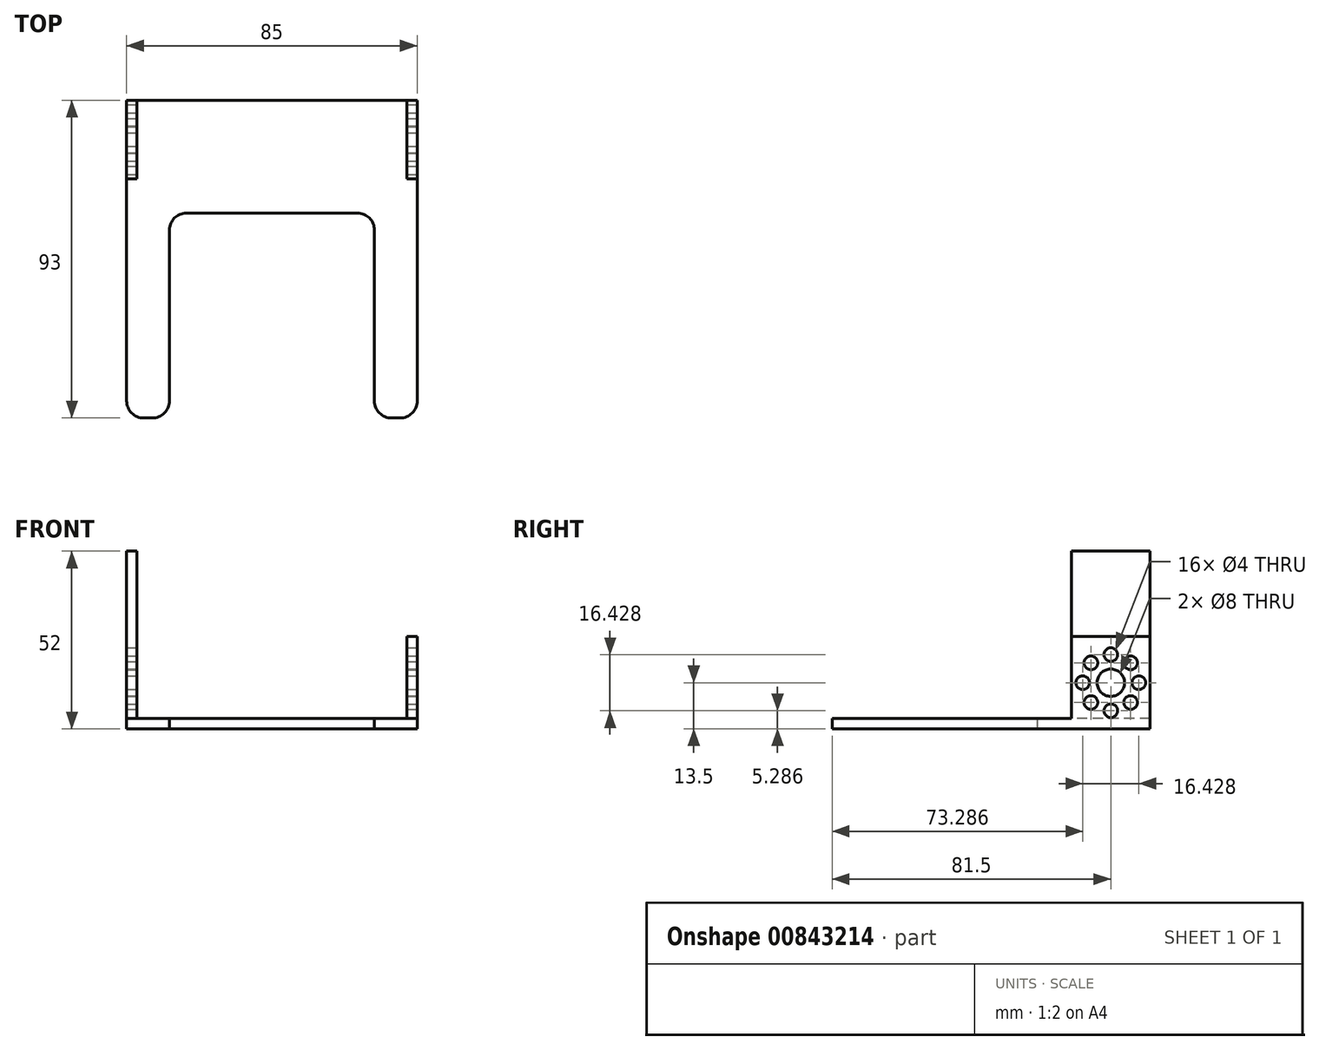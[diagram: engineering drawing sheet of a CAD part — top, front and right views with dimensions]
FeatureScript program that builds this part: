
annotation { "Feature Type Name" : "Feature", "Feature Type Description" : "" }
export const myFeature = defineFeature(function(context is Context, id is Id, definition is map)
    precondition{}
    {
        {
            var Q0;
            Q0=qCreatedBy(makeId("Top.planeOp"),FACE);
            var sketch = newSketch(context, id + "F0", { "sketchPlane" : qUnion([Q0])});
            skLineSegment(sketch, "E0.bottom", {"start": v(0, 0) * mm, "end": v(85, 0) * mm});
            skLineSegment(sketch, "E0.top", {"start": v(0, 23) * mm, "end": v(85, 23) * mm});
            skLineSegment(sketch, "E0.left", {"start": v(0, 0) * mm, "end": v(0, 23) * mm});
            skLineSegment(sketch, "E0.right", {"start": v(85, 0) * mm, "end": v(85, 23) * mm});
            skLineSegment(sketch, "E1.top", {"start": v(17.5, -10) * mm, "end": v(67.5, -10) * mm});
            skLineSegment(sketch, "E1.left", {"start": v(0, 0) * mm, "end": v(0, -10) * mm});
            skLineSegment(sketch, "E1.right", {"start": v(85, 0) * mm, "end": v(85, -10) * mm});
            skLineSegment(sketch, "E2.top", {"start": v(5, -70) * mm, "end": v(7.5, -70) * mm});
            skLineSegment(sketch, "E2.left", {"start": v(0, -10) * mm, "end": v(0, -65) * mm});
            skLineSegment(sketch, "E2.right", {"start": v(12.5, -15) * mm, "end": v(12.5, -65) * mm});
            skLineSegment(sketch, "E3.top", {"start": v(80, -70) * mm, "end": v(77.5, -70) * mm});
            skLineSegment(sketch, "E3.left", {"start": v(85, -10) * mm, "end": v(85, -65) * mm});
            skLineSegment(sketch, "E3.right", {"start": v(72.5, -15) * mm, "end": v(72.5, -65) * mm});
            skPoint(sketch, "E4.visualSharp", {"position": v(12.5, -70) * mm});
            skArc(sketch, "E4.filletArc", {"start": v(7.5, -70) * mm, "mid": v(11.04, -68.54) * mm, "end": v(12.5, -65) * mm});
            skPoint(sketch, "E5.visualSharp", {"position": v(0, -70) * mm});
            skArc(sketch, "E5.filletArc", {"start": v(0, -65) * mm, "mid": v(1.46, -68.54) * mm, "end": v(5, -70) * mm});
            skPoint(sketch, "E6.visualSharp", {"position": v(72.5, -70) * mm});
            skArc(sketch, "E6.filletArc", {"start": v(72.5, -65) * mm, "mid": v(73.96, -68.54) * mm, "end": v(77.5, -70) * mm});
            skPoint(sketch, "E7.visualSharp", {"position": v(85, -70) * mm});
            skArc(sketch, "E7.filletArc", {"start": v(80, -70) * mm, "mid": v(83.54, -68.54) * mm, "end": v(85, -65) * mm});
            skPoint(sketch, "E8.visualSharp", {"position": v(12.5, -10) * mm});
            skArc(sketch, "E8.filletArc", {"start": v(17.5, -10) * mm, "mid": v(13.96, -11.46) * mm, "end": v(12.5, -15) * mm});
            skPoint(sketch, "E9.visualSharp", {"position": v(72.5, -10) * mm});
            skArc(sketch, "E9.filletArc", {"start": v(72.5, -15) * mm, "mid": v(71.04, -11.46) * mm, "end": v(67.5, -10) * mm});
            skSolve(sketch);
        }
        {
            var Q0;
            Q0=qSketchRegion(id+"F0",true);
            extrude(context, id + "F1", {"entities" : qUnion([Q0]), "depth" : 3 * mm, "offsetDistance" : 25 * mm});
        }
        {
            var Q0;
            Q0=makeQuery(id+"F1.opExtrude","CAP_FACE",FACE,{"disambiguationData":[OSD([sQuery(id+"F0.wireOp",EDGE,"E0.bottom"),sQuery(id+"F0.wireOp",EDGE,"E0.top"),sQuery(id+"F0.wireOp",EDGE,"E0.left"),sQuery(id+"F0.wireOp",EDGE,"E0.right")])],"isStart":false});
            var sketch = newSketch(context, id + "F2", { "sketchPlane" : qUnion([Q0])});
            skLineSegment(sketch, "E10.bottom", {"start": v(0, 23) * mm, "end": v(3, 23) * mm});
            skLineSegment(sketch, "E10.top", {"start": v(0, 0) * mm, "end": v(3, 0) * mm});
            skLineSegment(sketch, "E10.left", {"start": v(0, 23) * mm, "end": v(0, 0) * mm});
            skLineSegment(sketch, "E10.right", {"start": v(3, 23) * mm, "end": v(3, 0) * mm});
            skLineSegment(sketch, "E11.bottom", {"start": v(85, 23) * mm, "end": v(82, 23) * mm});
            skLineSegment(sketch, "E11.top", {"start": v(85, 0) * mm, "end": v(82, 0) * mm});
            skLineSegment(sketch, "E11.left", {"start": v(85, 23) * mm, "end": v(85, 0) * mm});
            skLineSegment(sketch, "E11.right", {"start": v(82, 23) * mm, "end": v(82, 0) * mm});
            skSolve(sketch);
        }
        {
            var Q0;
            Q0=qSketchRegion(id+"F2",true);
            extrude(context, id + "F3", {"entities" : qUnion([Q0]), "operationType" : NewBodyOperationType.ADD, "depth" : 24 * mm, "offsetDistance" : 25 * mm});
        }
        {
            var Q0;
            Q0=makeQuery(id+"F3.opExtrude","CAP_FACE",FACE,{"disambiguationData":[OSD([sQuery(id+"F2.wireOp",EDGE,"E10.bottom"),sQuery(id+"F2.wireOp",EDGE,"E10.top"),sQuery(id+"F2.wireOp",EDGE,"E10.left"),sQuery(id+"F2.wireOp",EDGE,"E10.right")])],"isStart":false});
            var sketch = newSketch(context, id + "F4", { "sketchPlane" : qUnion([Q0])});
            skLineSegment(sketch, "E12.bottom", {"start": v(0, 23) * mm, "end": v(3, 23) * mm});
            skLineSegment(sketch, "E12.top", {"start": v(0, 0) * mm, "end": v(3, 0) * mm});
            skLineSegment(sketch, "E12.left", {"start": v(0, 23) * mm, "end": v(0, 0) * mm});
            skLineSegment(sketch, "E12.right", {"start": v(3, 23) * mm, "end": v(3, 0) * mm});
            skSolve(sketch);
        }
        {
            var Q0;
            Q0=qSketchRegion(id+"F4",true);
            extrude(context, id + "F5", {"entities" : qUnion([Q0]), "operationType" : NewBodyOperationType.ADD, "depth" : 25 * mm, "offsetDistance" : 25 * mm});
        }
        {
            var Q0;
            Q0=makeQuery(id+"F3.boolean.opBoolean","MERGE",FACE,{"derivedFrom":[makeQuery(id+"F1.opExtrude","SWEPT_FACE",FACE,{"disambiguationData":[OSD([sQuery(id+"F0.wireOp",EDGE,"E0.right"),sQuery(id+"F0.wireOp",EDGE,"E1.right"),sQuery(id+"F0.wireOp",EDGE,"E3.left")])]}),makeQuery(id+"F3.opExtrude","SWEPT_FACE",FACE,{"disambiguationData":[OSD([sQuery(id+"F2.wireOp",EDGE,"E11.left")])]})]});
            var sketch = newSketch(context, id + "F6", { "sketchPlane" : qUnion([Q0])});
            skCircle(sketch, "E13", {"center": v(11.5, 13.5) * mm, "radius": 4 * mm});
            skCircle(sketch, "E14", {"center": v(19.71, 13.5) * mm, "radius": 2 * mm});
            skCircle(sketch, "E15.1.0", {"center": v(17.3, 19.3) * mm, "radius": 2 * mm});
            skCircle(sketch, "E15.2.0", {"center": v(11.5, 21.71) * mm, "radius": 2 * mm});
            skCircle(sketch, "E15.3.0", {"center": v(5.7, 19.3) * mm, "radius": 2 * mm});
            skCircle(sketch, "E15.4.0", {"center": v(3.29, 13.5) * mm, "radius": 2 * mm});
            skCircle(sketch, "E15.5.0", {"center": v(5.7, 7.7) * mm, "radius": 2 * mm});
            skCircle(sketch, "E15.6.0", {"center": v(11.5, 5.29) * mm, "radius": 2 * mm});
            skCircle(sketch, "E15.7.0", {"center": v(17.3, 7.7) * mm, "radius": 2 * mm});
            skSolve(sketch);
        }
        {
            var Q0;
            Q0 = qSketchRegion(id + "F6", true);
            extrude(context, id + "F7", {"entities" : qUnion([Q0]), "operationType" : NewBodyOperationType.REMOVE, "oppositeDirection" : true, "depth" : 100 * mm, "offsetDistance" : 25 * mm});
        }
    });
